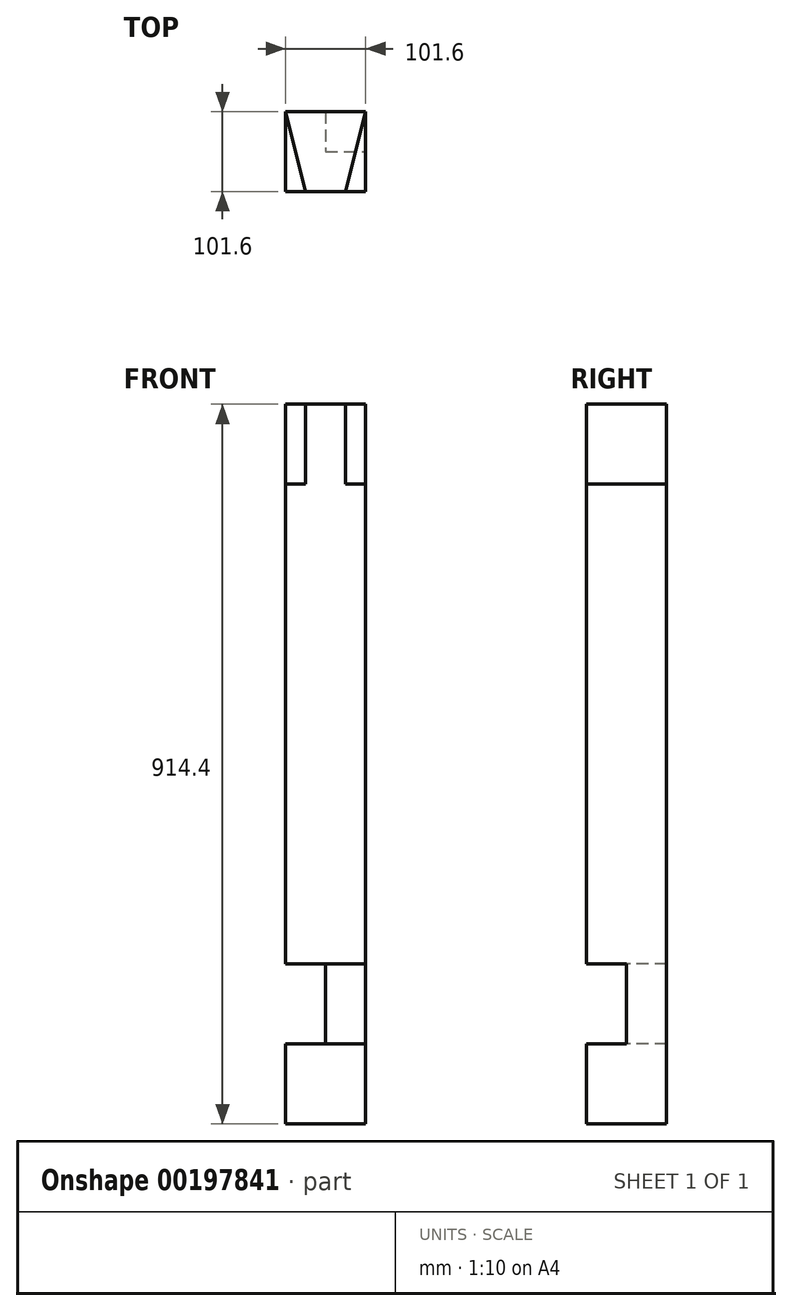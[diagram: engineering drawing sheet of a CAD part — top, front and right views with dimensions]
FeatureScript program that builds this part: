
annotation { "Feature Type Name" : "Feature", "Feature Type Description" : "" }
export const myFeature = defineFeature(function(context is Context, id is Id, definition is map)
    precondition{}
    {
        {
            var Q0;
            Q0=qCreatedBy(makeId("Top.planeOp"),FACE);
            var sketch = newSketch(context, id + "F0", { "sketchPlane" : qUnion([Q0])});
            skLineSegment(sketch, "E0.bottom", {"start": v(50.8, -50.8) * mm, "end": v(-50.8, -50.8) * mm});
            skLineSegment(sketch, "E0.top", {"start": v(50.8, 50.8) * mm, "end": v(-50.8, 50.8) * mm});
            skLineSegment(sketch, "E0.left", {"start": v(50.8, -50.8) * mm, "end": v(50.8, 50.8) * mm});
            skLineSegment(sketch, "E0.right", {"start": v(-50.8, -50.8) * mm, "end": v(-50.8, 50.8) * mm});
            skPoint(sketch, "E0.middle", {"position": v(0, 0) * mm});
            skSolve(sketch);
        }
        {
            var Q0;
            Q0=makeQuery(id+"F0.imprint","IMPRINT",FACE,{"disambiguationData":[TD([[makeQuery(id+"F0.imprint","IMPRINT",EDGE,{"derivedFrom":sQuery(id+"F0.wireOp",EDGE,"E0.bottom")}),-1.0]])]});
            extrude(context, id + "F1", {"entities" : qUnion([Q0]), "depth" : 914.4 * mm});
        }
        {
            var Q0;
            Q0=makeQuery(id+"F1.opExtrude","CAP_FACE",FACE,{"disambiguationData":[OSD([sQuery(id+"F0.wireOp",EDGE,"E0.bottom"),sQuery(id+"F0.wireOp",EDGE,"E0.top"),sQuery(id+"F0.wireOp",EDGE,"E0.left"),sQuery(id+"F0.wireOp",EDGE,"E0.right")])],"isStart":false});
            var sketch = newSketch(context, id + "F2", { "sketchPlane" : qUnion([Q0])});
            skLineSegment(sketch, "E1", {"start": v(-50.8, 50.8) * mm, "end": v(-25.4, -50.8) * mm});
            skLineSegment(sketch, "E2", {"start": v(0, 50.8) * mm, "end": v(0, -50.8) * mm, "construction": true});
            skLineSegment(sketch, "E3.MirrorCS", {"start": v(50.8, 50.8) * mm, "end": v(25.4, -50.8) * mm});
            skLineSegment(sketch, "E4", {"start": v(-50.8, 50.8) * mm, "end": v(50.8, 50.8) * mm});
            skLineSegment(sketch, "E5", {"start": v(25.4, -50.8) * mm, "end": v(-25.4, -50.8) * mm});
            skSolve(sketch);
        }
        {
            var Q0;
            {var subQ0=sQuery(id+"F2.wireOp",EDGE,"E1");Q0=makeQuery(id+"F2.imprint","IMPRINT",FACE,{"disambiguationData":[TD([[makeQuery(id+"F2.imprint","IMPRINT",EDGE,{"derivedFrom":subQ0}),-1.0]])]});}
            var Q1;
            {var subQ0=sQuery(id+"F2.wireOp",EDGE,"E3.MirrorCS");Q1=makeQuery(id+"F2.imprint","IMPRINT",FACE,{"disambiguationData":[TD([[makeQuery(id+"F2.imprint","IMPRINT",EDGE,{"derivedFrom":subQ0}),1.0]])]});}
            extrude(context, id + "F3", {"entities" : qUnion([Q0, Q1]), "operationType" : NewBodyOperationType.REMOVE, "oppositeDirection" : true, "depth" : 101.6 * mm});
        }
        {
            var Q0;
            Q0=makeQuery(id+"F1.opExtrude","SWEPT_FACE",FACE,{"disambiguationData":[OSD([sQuery(id+"F0.wireOp",EDGE,"E0.bottom")])]});
            var sketch = newSketch(context, id + "F4", { "sketchPlane" : qUnion([Q0])});
            skLineSegment(sketch, "E6.bottom", {"start": v(-50.8, 203.2) * mm, "end": v(50.8, 203.2) * mm});
            skLineSegment(sketch, "E6.top", {"start": v(-50.8, 101.6) * mm, "end": v(50.8, 101.6) * mm});
            skLineSegment(sketch, "E6.left", {"start": v(-50.8, 203.2) * mm, "end": v(-50.8, 101.6) * mm});
            skLineSegment(sketch, "E6.right", {"start": v(50.8, 203.2) * mm, "end": v(50.8, 101.6) * mm});
            skSolve(sketch);
        }
        {
            var Q0;
            Q0=makeQuery(id+"F4.imprint","IMPRINT",FACE,{"disambiguationData":[TD([[makeQuery(id+"F4.imprint","IMPRINT",EDGE,{"derivedFrom":sQuery(id+"F4.wireOp",EDGE,"E6.bottom")}),-1.0]])]});
            extrude(context, id + "F5", {"entities" : qUnion([Q0]), "operationType" : NewBodyOperationType.REMOVE, "oppositeDirection" : true, "depth" : 50.8 * mm});
        }
        {
            var Q0;
            Q0=makeQuery(id+"F1.opExtrude","SWEPT_FACE",FACE,{"disambiguationData":[OSD([sQuery(id+"F0.wireOp",EDGE,"E0.right")])]});
            var sketch = newSketch(context, id + "F6", { "sketchPlane" : qUnion([Q0])});
            skLineSegment(sketch, "E7.bottom", {"start": v(-50.8, 203.2) * mm, "end": v(50.8, 203.2) * mm});
            skLineSegment(sketch, "E7.top", {"start": v(-50.8, 101.6) * mm, "end": v(50.8, 101.6) * mm});
            skLineSegment(sketch, "E7.left", {"start": v(-50.8, 203.2) * mm, "end": v(-50.8, 101.6) * mm});
            skLineSegment(sketch, "E7.right", {"start": v(50.8, 203.2) * mm, "end": v(50.8, 101.6) * mm});
            skSolve(sketch);
        }
        {
            var Q0;
            Q0=makeQuery(id+"F6.imprint","IMPRINT",FACE,{"disambiguationData":[TD([[makeQuery(id+"F6.imprint","IMPRINT",EDGE,{"derivedFrom":sQuery(id+"F6.wireOp",EDGE,"E7.bottom")}),-1.0]])]});
            extrude(context, id + "F7", {"entities" : qUnion([Q0]), "operationType" : NewBodyOperationType.REMOVE, "oppositeDirection" : true, "depth" : 50.8 * mm});
        }
    });
